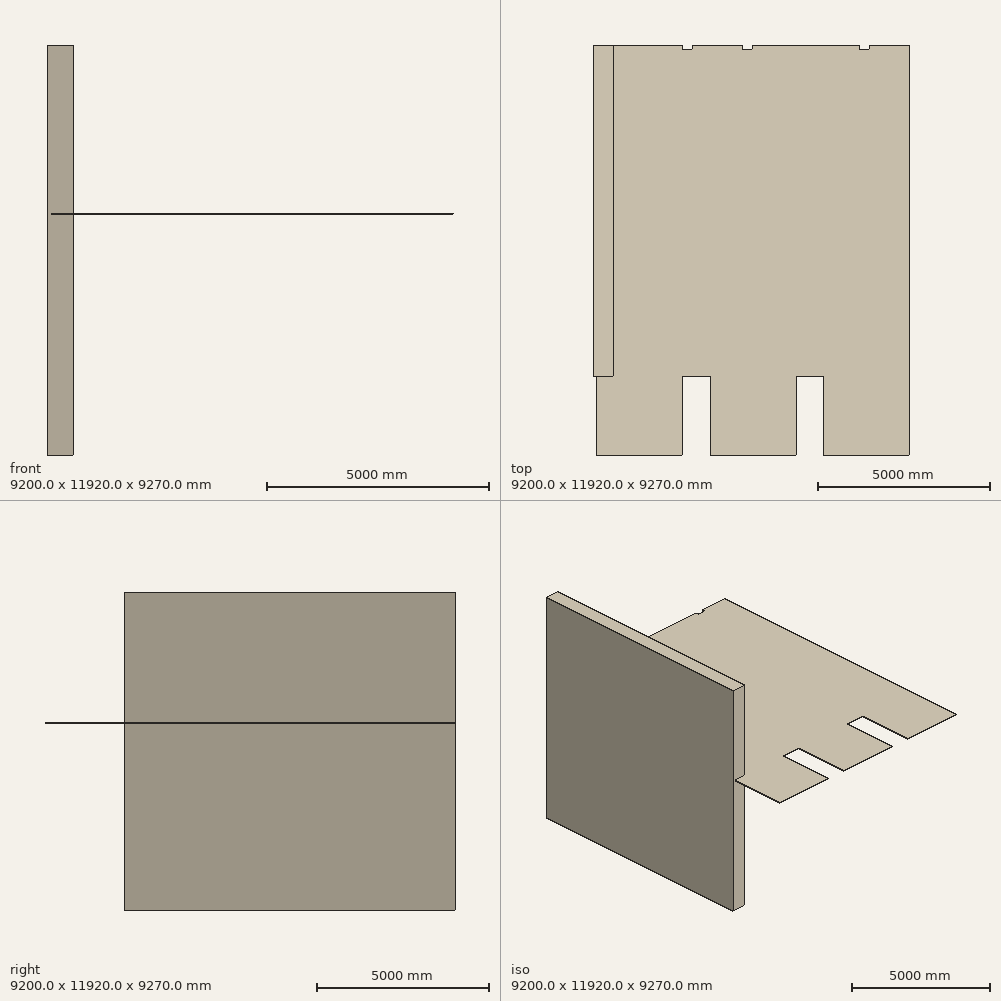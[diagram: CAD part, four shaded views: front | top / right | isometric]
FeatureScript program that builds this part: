
annotation { "Feature Type Name" : "Feature", "Feature Type Description" : "" }
export const myFeature = defineFeature(function(context is Context, id is Id, definition is map)
    precondition{}
    {
        {
            var Q0;
            Q0=qCreatedBy(makeId("Top.planeOp"),FACE);
            var sketch = newSketch(context, id + "F0", { "sketchPlane" : qUnion([Q0])});
            skLineSegment(sketch, "E0.bottom", {"start": v(-2500, 0) * mm, "end": v(-3300, 0) * mm});
            skLineSegment(sketch, "E0.top", {"start": v(0, 9620) * mm, "end": v(-1180, 9620) * mm});
            skLineSegment(sketch, "E0.left", {"start": v(0, 0) * mm, "end": v(0, 9620) * mm});
            skLineSegment(sketch, "E0.right", {"start": v(-8600, 0) * mm, "end": v(-8600, 9620) * mm});
            skLineSegment(sketch, "E1.top", {"start": v(0, -2300) * mm, "end": v(-2500, -2300) * mm});
            skLineSegment(sketch, "E1.left", {"start": v(0, 0) * mm, "end": v(0, -2300) * mm});
            skLineSegment(sketch, "E1.right", {"start": v(-2500, 0) * mm, "end": v(-2500, -2300) * mm});
            skLineSegment(sketch, "E2.left", {"start": v(-2500, -2300) * mm, "end": v(-2500, 0) * mm});
            skLineSegment(sketch, "E2.right", {"start": v(-3300, -2300) * mm, "end": v(-3300, 0) * mm});
            skLineSegment(sketch, "E3.top", {"start": v(-3300, -2300) * mm, "end": v(-5800, -2300) * mm});
            skLineSegment(sketch, "E3.left", {"start": v(-3300, 0) * mm, "end": v(-3300, -2300) * mm});
            skLineSegment(sketch, "E3.right", {"start": v(-5800, 0) * mm, "end": v(-5800, -2300) * mm});
            skLineSegment(sketch, "E4.bottom", {"start": v(-5800, 0) * mm, "end": v(-6600, 0) * mm});
            skLineSegment(sketch, "E4.right", {"start": v(-6600, 0) * mm, "end": v(-6600, -2300) * mm});
            skLineSegment(sketch, "E5.bottom", {"start": v(-8600, 0) * mm, "end": v(-9100, 0) * mm});
            skLineSegment(sketch, "E5.top", {"start": v(-6600, -2300) * mm, "end": v(-9100, -2300) * mm});
            skLineSegment(sketch, "E5.right", {"start": v(-9100, 0) * mm, "end": v(-9100, -2300) * mm});
            skLineSegment(sketch, "E6.top", {"start": v(-1180, 9490) * mm, "end": v(-1470, 9490) * mm});
            skLineSegment(sketch, "E6.left", {"start": v(-1180, 9620) * mm, "end": v(-1180, 9490) * mm});
            skLineSegment(sketch, "E6.right", {"start": v(-1470, 9620) * mm, "end": v(-1470, 9490) * mm});
            skLineSegment(sketch, "E7.top", {"start": v(-4570, 9490) * mm, "end": v(-4860, 9490) * mm});
            skLineSegment(sketch, "E7.left", {"start": v(-4570, 9620) * mm, "end": v(-4570, 9490) * mm});
            skLineSegment(sketch, "E7.right", {"start": v(-4860, 9620) * mm, "end": v(-4860, 9490) * mm});
            skLineSegment(sketch, "E8.top", {"start": v(-6600, 9490) * mm, "end": v(-6310, 9490) * mm});
            skLineSegment(sketch, "E8.left", {"start": v(-6600, 9620) * mm, "end": v(-6600, 9490) * mm});
            skLineSegment(sketch, "E8.right", {"start": v(-6310, 9620) * mm, "end": v(-6310, 9490) * mm});
            skLineSegment(sketch, "E9.trimOffspring", {"start": v(-6600, 9620) * mm, "end": v(-8600, 9620) * mm});
            skLineSegment(sketch, "E10.trimOffspring", {"start": v(-4860, 9620) * mm, "end": v(-6310, 9620) * mm});
            skLineSegment(sketch, "E11.trimOffspring", {"start": v(-1470, 9620) * mm, "end": v(-4570, 9620) * mm});
            skSolve(sketch);
        }
        {
            var Q0;
            Q0=makeQuery(id+"F0.imprint","IMPRINT",FACE,{"disambiguationData":[TD([[makeQuery(id+"F0.imprint","IMPRINT",EDGE,{"derivedFrom":sQuery(id+"F0.wireOp",EDGE,"E0.top")}),1.0]])]});
            var Q1;
            Q1=makeQuery(id+"F0.imprint","IMPRINT",FACE,{"disambiguationData":[TD([[makeQuery(id+"F0.imprint","IMPRINT",EDGE,{"derivedFrom":sQuery(id+"F0.wireOp",EDGE,"E5.top")}),-1.0]])]});
            var Q2;
            Q2=makeQuery(id+"F0.imprint","IMPRINT",FACE,{"disambiguationData":[TD([[makeQuery(id+"F0.imprint","IMPRINT",EDGE,{"derivedFrom":sQuery(id+"F0.wireOp",EDGE,"E3.bottom")}),1.0]])]});
            var Q3;
            Q3=makeQuery(id+"F0.imprint","IMPRINT",FACE,{"disambiguationData":[TD([[makeQuery(id+"F0.imprint","IMPRINT",EDGE,{"derivedFrom":sQuery(id+"F0.wireOp",EDGE,"E1.bottom")}),1.0]])]});
            extrude(context, id + "F1", {"entities" : qUnion([Q0, Q1, Q2, Q3]), "depth" : 25 * mm, "offsetDistance" : 25 * mm});
        }
        {
            var Q0;
            Q0=makeQuery(id+"F1.opExtrude","CAP_FACE",FACE,{"disambiguationData":[OSD([sQuery(id+"F0.wireOp",EDGE,"E0.top"),sQuery(id+"F0.wireOp",EDGE,"E0.left"),sQuery(id+"F0.wireOp",EDGE,"E0.right"),sQuery(id+"F0.wireOp",EDGE,"E1.top"),sQuery(id+"F0.wireOp",EDGE,"E1.left"),sQuery(id+"F0.wireOp",EDGE,"E0.bottom"),sQuery(id+"F0.wireOp",EDGE,"E2.left"),sQuery(id+"F0.wireOp",EDGE,"E3.top"),sQuery(id+"F0.wireOp",EDGE,"E3.left"),sQuery(id+"F0.wireOp",EDGE,"E3.right"),sQuery(id+"F0.wireOp",EDGE,"E5.bottom"),sQuery(id+"F0.wireOp",EDGE,"E5.top"),sQuery(id+"F0.wireOp",EDGE,"E4.right"),sQuery(id+"F0.wireOp",EDGE,"E5.right"),sQuery(id+"F0.wireOp",EDGE,"E6.top"),sQuery(id+"F0.wireOp",EDGE,"E6.left"),sQuery(id+"F0.wireOp",EDGE,"E6.right"),sQuery(id+"F0.wireOp",EDGE,"E7.top"),sQuery(id+"F0.wireOp",EDGE,"E7.left"),sQuery(id+"F0.wireOp",EDGE,"E7.right"),sQuery(id+"F0.wireOp",EDGE,"E8.top"),sQuery(id+"F0.wireOp",EDGE,"E8.left"),sQuery(id+"F0.wireOp",EDGE,"E8.right"),sQuery(id+"F0.wireOp",EDGE,"E4.bottom"),sQuery(id+"F0.wireOp",EDGE,"E9.trimOffspring"),sQuery(id+"F0.wireOp",EDGE,"E10.trimOffspring"),sQuery(id+"F0.wireOp",EDGE,"E11.trimOffspring")])],"isStart":false});
            var sketch = newSketch(context, id + "F2", { "sketchPlane" : qUnion([Q0])});
            skLineSegment(sketch, "E12.bottom", {"start": v(-8600, 9620) * mm, "end": v(-9200, 9620) * mm});
            skLineSegment(sketch, "E12.top", {"start": v(-8600, 0) * mm, "end": v(-9200, 0) * mm});
            skLineSegment(sketch, "E12.left", {"start": v(-8600, 9620) * mm, "end": v(-8600, 0) * mm});
            skLineSegment(sketch, "E12.right", {"start": v(-9200, 9620) * mm, "end": v(-9200, 0) * mm});
            skSolve(sketch);
        }
        {
            var Q0;
            Q0=makeQuery(id+"F2.imprint","IMPRINT",FACE,{"disambiguationData":[TD([[makeQuery(id+"F2.imprint","IMPRINT",EDGE,{"derivedFrom":sQuery(id+"F2.wireOp",EDGE,"FqwyhctI-YljK-LCXx-xCG9-kKrhjtetXPhs.bottom")}),1.0]])]});
            var Q1;
            Q1=makeQuery(id+"F2.imprint","IMPRINT",FACE,{"disambiguationData":[TD([[makeQuery(id+"F2.imprint","IMPRINT",EDGE,{"derivedFrom":sQuery(id+"F2.wireOp",EDGE,"E12.bottom")}),1.0]])]});
            extrude(context, id + "F3", {"entities" : qUnion([Q0, Q1]), "oppositeDirection" : true, "depth" : 5470 * mm, "offsetDistance" : 25 * mm});
        }
        {
            var Q0;
            Q0=makeQuery(id+"F3.opExtrude","CAP_FACE",FACE,{"disambiguationData":[OSD([sQuery(id+"F2.wireOp",EDGE,"E12.bottom"),sQuery(id+"F2.wireOp",EDGE,"E12.top"),sQuery(id+"F2.wireOp",EDGE,"E12.left"),sQuery(id+"F2.wireOp",EDGE,"E12.right")])],"isStart":false});
            extrude(context, id + "F4", {"entities" : qUnion([Q0]), "operationType" : NewBodyOperationType.ADD, "oppositeDirection" : true, "depth" : 9270 * mm, "offsetDistance" : 25 * mm});
        }
    });
